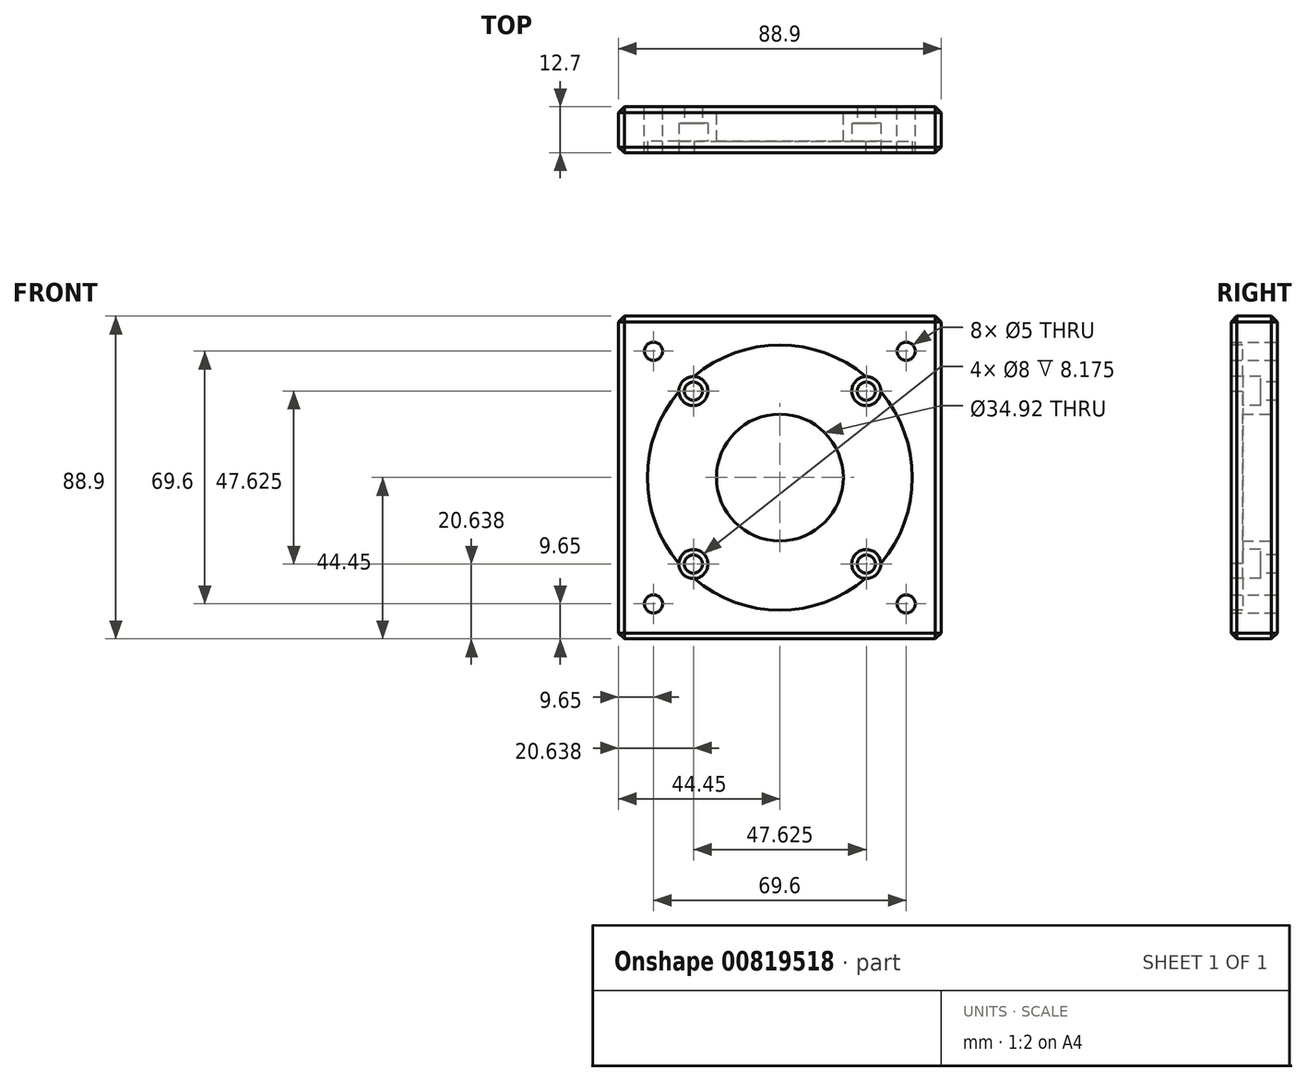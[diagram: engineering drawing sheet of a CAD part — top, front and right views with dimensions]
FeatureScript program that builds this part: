
annotation { "Feature Type Name" : "Feature", "Feature Type Description" : "" }
export const myFeature = defineFeature(function(context is Context, id is Id, definition is map)
    precondition{}
    {
        {
            var Q0;
            Q0=qCreatedBy(makeId("Front.planeOp"),FACE);
            var sketch = newSketch(context, id + "F0", { "sketchPlane" : qUnion([Q0])});
            skLineSegment(sketch, "E0.bottom", {"start": v(-44.45, 44.45) * mm, "end": v(44.45, 44.45) * mm});
            skLineSegment(sketch, "E0.top", {"start": v(-44.45, -44.45) * mm, "end": v(44.45, -44.45) * mm});
            skLineSegment(sketch, "E0.left", {"start": v(-44.45, 44.45) * mm, "end": v(-44.45, -44.45) * mm});
            skLineSegment(sketch, "E0.right", {"start": v(44.45, 44.45) * mm, "end": v(44.45, -44.45) * mm});
            skLineSegment(sketch, "E1", {"start": v(-44.45, 44.45) * mm, "end": v(44.45, -44.45) * mm, "construction": true});
            skLineSegment(sketch, "E2", {"start": v(44.45, 44.45) * mm, "end": v(-44.45, -44.45) * mm, "construction": true});
            skCircle(sketch, "E3", {"center": v(0, 0) * mm, "radius": 17.46 * mm});
            skCircle(sketch, "E4", {"center": v(-34.8, 34.8) * mm, "radius": 2.5 * mm});
            skCircle(sketch, "E5", {"center": v(34.8, 34.8) * mm, "radius": 2.5 * mm});
            skCircle(sketch, "E6", {"center": v(34.8, -34.8) * mm, "radius": 2.5 * mm});
            skCircle(sketch, "E7", {"center": v(-34.8, -34.8) * mm, "radius": 2.5 * mm});
            skLineSegment(sketch, "E8", {"start": v(-34.8, 34.8) * mm, "end": v(34.8, 34.8) * mm, "construction": true});
            skLineSegment(sketch, "E9", {"start": v(34.8, 34.8) * mm, "end": v(34.8, -34.8) * mm, "construction": true});
            skLineSegment(sketch, "E10", {"start": v(34.8, -34.8) * mm, "end": v(-34.8, -34.8) * mm, "construction": true});
            skLineSegment(sketch, "E11", {"start": v(-34.8, -34.8) * mm, "end": v(-34.8, 34.8) * mm, "construction": true});
            skSolve(sketch);
        }
        {
            var Q0;
            Q0=makeQuery(id+"F0.imprint","IMPRINT",FACE,{"disambiguationData":[TD([[makeQuery(id+"F0.imprint","IMPRINT",EDGE,{"derivedFrom":sQuery(id+"F0.wireOp",EDGE,"E0.bottom")}),-1.0]])]});
            extrude(context, id + "F1", {"entities" : qUnion([Q0]), "depth" : 12.7 * mm, "offsetDistance" : 25.4 * mm});
        }
        {
            var Q0;
            Q0=makeQuery(id+"F1.opExtrude","CAP_FACE",FACE,{"disambiguationData":[OSD([sQuery(id+"F0.wireOp",EDGE,"E0.bottom"),sQuery(id+"F0.wireOp",EDGE,"E0.top"),sQuery(id+"F0.wireOp",EDGE,"E0.left"),sQuery(id+"F0.wireOp",EDGE,"E0.right"),sQuery(id+"F0.wireOp",EDGE,"E3"),sQuery(id+"F0.wireOp",EDGE,"E4"),sQuery(id+"F0.wireOp",EDGE,"E5"),sQuery(id+"F0.wireOp",EDGE,"E6"),sQuery(id+"F0.wireOp",EDGE,"E7")])],"isStart":false});
            var sketch = newSketch(context, id + "F2", { "sketchPlane" : qUnion([Q0])});
            skCircle(sketch, "E12", {"center": v(0, 0) * mm, "radius": 36.51 * mm});
            skSolve(sketch);
        }
        {
            var Q0;
            Q0 = qSketchRegion(id + "F2", true);
            extrude(context, id + "F3", {"entities" : qUnion([Q0]), "operationType" : NewBodyOperationType.REMOVE, "oppositeDirection" : true, "depth" : 3.17 * mm, "offsetDistance" : 25.4 * mm});
        }
        {
            var Q0;
            Q0=makeQuery(id+"F1.opExtrude","CAP_FACE",FACE,{"disambiguationData":[OSD([sQuery(id+"F0.wireOp",EDGE,"E0.bottom"),sQuery(id+"F0.wireOp",EDGE,"E0.top"),sQuery(id+"F0.wireOp",EDGE,"E0.left"),sQuery(id+"F0.wireOp",EDGE,"E0.right"),sQuery(id+"F0.wireOp",EDGE,"E3"),sQuery(id+"F0.wireOp",EDGE,"E4"),sQuery(id+"F0.wireOp",EDGE,"E5"),sQuery(id+"F0.wireOp",EDGE,"E6"),sQuery(id+"F0.wireOp",EDGE,"E7")])],"isStart":false});
            var sketch = newSketch(context, id + "F4", { "sketchPlane" : qUnion([Q0])});
            skLineSegment(sketch, "E13", {"start": v(-23.81, 23.81) * mm, "end": v(23.81, 23.81) * mm, "construction": true});
            skLineSegment(sketch, "E14", {"start": v(23.81, 23.81) * mm, "end": v(23.81, -23.81) * mm, "construction": true});
            skLineSegment(sketch, "E15", {"start": v(23.81, -23.81) * mm, "end": v(-23.81, -23.81) * mm, "construction": true});
            skLineSegment(sketch, "E16", {"start": v(-23.81, -23.81) * mm, "end": v(-23.81, 23.81) * mm, "construction": true});
            skLineSegment(sketch, "E17", {"start": v(-23.81, 23.81) * mm, "end": v(23.81, -23.81) * mm, "construction": true});
            skLineSegment(sketch, "E18", {"start": v(23.81, 23.81) * mm, "end": v(-23.81, -23.81) * mm, "construction": true});
            skSolve(sketch);
        }
        {
            var Q0;
            Q0=sQuery(id+"F4.wireOp",VERTEX,"E13.start");
            var Q1;
            Q1=sQuery(id+"F4.wireOp",VERTEX,"E13.end");
            var Q2;
            Q2=sQuery(id+"F4.wireOp",VERTEX,"E14.end");
            var Q3;
            Q3=sQuery(id+"F4.wireOp",VERTEX,"E15.end");
            var Q4;
            Q4=makeQuery(id+"F1.opExtrude","SWEPT_BODY",BODY,{"disambiguationData":[OSD([sQuery(id+"F0.wireOp",EDGE,"E0.bottom"),sQuery(id+"F0.wireOp",EDGE,"E0.top"),sQuery(id+"F0.wireOp",EDGE,"E0.left"),sQuery(id+"F0.wireOp",EDGE,"E0.right"),sQuery(id+"F0.wireOp",EDGE,"E3"),sQuery(id+"F0.wireOp",EDGE,"E4"),sQuery(id+"F0.wireOp",EDGE,"E5"),sQuery(id+"F0.wireOp",EDGE,"E6"),sQuery(id+"F0.wireOp",EDGE,"E7")])]});
            hole(context, id + "F5", {"style" : HoleStyle.C_BORE, "endStyle" : HoleEndStyle.THROUGH, "holeDiameter" : 5 * mm, "cBoreDiameter" : 8 * mm, "cBoreDepth" : 5 * mm, "majorDiameter" : 6.35 * mm, "isTappedThrough" : true, "tappedDepth" : 12.7 * mm, "tapClearance" : 3, "locations" : qUnion([Q0, Q1, Q2, Q3]), "scope" : qUnion([Q4])});
        }
        {
            var Q0;
            Q0=makeQuery(id+"F1.opExtrude","CAP_EDGE",EDGE,{"disambiguationData":[OSD([sQuery(id+"F0.wireOp",EDGE,"E0.bottom")])],"isStart":false});
            var Q1;
            Q1=makeQuery(id+"F1.opExtrude","CAP_EDGE",EDGE,{"disambiguationData":[OSD([sQuery(id+"F0.wireOp",EDGE,"E0.left")])],"isStart":false});
            var Q2;
            Q2=makeQuery(id+"F1.opExtrude","CAP_EDGE",EDGE,{"disambiguationData":[OSD([sQuery(id+"F0.wireOp",EDGE,"E0.right")])],"isStart":false});
            var Q3;
            Q3=makeQuery(id+"F1.opExtrude","CAP_EDGE",EDGE,{"disambiguationData":[OSD([sQuery(id+"F0.wireOp",EDGE,"E0.top")])],"isStart":false});
            var Q4;
            Q4=makeQuery(id+"F1.opExtrude","CAP_EDGE",EDGE,{"disambiguationData":[OSD([sQuery(id+"F0.wireOp",EDGE,"E0.right")])],"isStart":true});
            var Q5;
            Q5=makeQuery(id+"F1.opExtrude","CAP_EDGE",EDGE,{"disambiguationData":[OSD([sQuery(id+"F0.wireOp",EDGE,"E0.top")])],"isStart":true});
            var Q6;
            Q6=makeQuery(id+"F1.opExtrude","CAP_EDGE",EDGE,{"disambiguationData":[OSD([sQuery(id+"F0.wireOp",EDGE,"E0.left")])],"isStart":true});
            var Q7;
            Q7=makeQuery(id+"F1.opExtrude","CAP_EDGE",EDGE,{"disambiguationData":[OSD([sQuery(id+"F0.wireOp",EDGE,"E0.bottom")])],"isStart":true});
            var Q8;
            Q8=makeQuery(id+"F1.opExtrude","SWEPT_EDGE",EDGE,{"disambiguationData":[OSD([sQuery(id+"F0.wireOp",EDGE,"E0.bottom"),sQuery(id+"F0.wireOp",EDGE,"E0.left")])]});
            var Q9;
            Q9=makeQuery(id+"F1.opExtrude","SWEPT_EDGE",EDGE,{"disambiguationData":[OSD([sQuery(id+"F0.wireOp",EDGE,"E0.top"),sQuery(id+"F0.wireOp",EDGE,"E0.left")])]});
            var Q10;
            Q10=makeQuery(id+"F1.opExtrude","SWEPT_EDGE",EDGE,{"disambiguationData":[OSD([sQuery(id+"F0.wireOp",EDGE,"E0.bottom"),sQuery(id+"F0.wireOp",EDGE,"E0.right")])]});
            var Q11;
            Q11=makeQuery(id+"F1.opExtrude","SWEPT_EDGE",EDGE,{"disambiguationData":[OSD([sQuery(id+"F0.wireOp",EDGE,"E0.top"),sQuery(id+"F0.wireOp",EDGE,"E0.right")])]});
            chamfer(context, id + "F6", {"entities" : qUnion([Q0, Q1, Q2, Q3, Q4, Q5, Q6, Q7, Q8, Q9, Q10, Q11]), "width" : 1.59 * mm, "tangentPropagation" : true});
        }
    });
